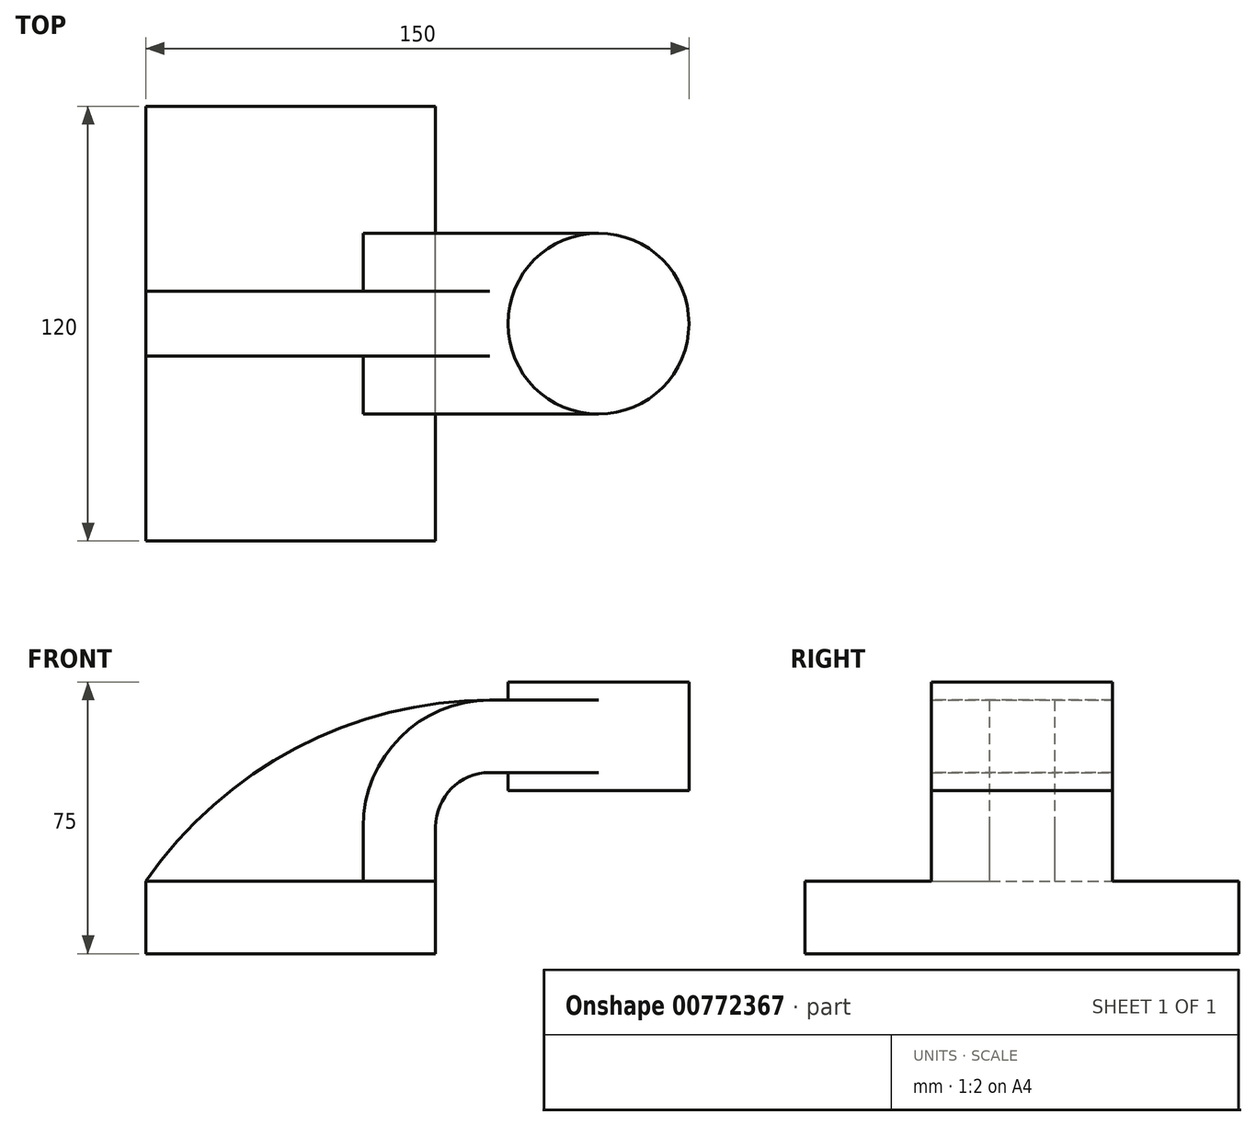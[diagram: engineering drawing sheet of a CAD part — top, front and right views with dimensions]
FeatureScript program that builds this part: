
annotation { "Feature Type Name" : "Feature", "Feature Type Description" : "" }
export const myFeature = defineFeature(function(context is Context, id is Id, definition is map)
    precondition{}
    {
        {
            var Q0;
            Q0=qCreatedBy(makeId("Front.planeOp"),FACE);
            var sketch = newSketch(context, id + "F0", { "sketchPlane" : qUnion([Q0])});
            skLineSegment(sketch, "E0", {"start": v(0, 0) * mm, "end": v(80, 0) * mm});
            skLineSegment(sketch, "E1", {"start": v(80, 0) * mm, "end": v(80, 20) * mm});
            skLineSegment(sketch, "E2", {"start": v(80, 20) * mm, "end": v(0, 20) * mm});
            skLineSegment(sketch, "E3", {"start": v(0, 20) * mm, "end": v(0, 0) * mm});
            skLineSegment(sketch, "E4", {"start": v(80, 20) * mm, "end": v(80, 35) * mm});
            skLineSegment(sketch, "E5", {"start": v(95, 50) * mm, "end": v(100, 50) * mm});
            skLineSegment(sketch, "E6", {"start": v(100, 50) * mm, "end": v(100, 45) * mm});
            skLineSegment(sketch, "E7", {"start": v(100, 45) * mm, "end": v(150, 45) * mm});
            skLineSegment(sketch, "E8", {"start": v(150, 45) * mm, "end": v(150, 75) * mm});
            skLineSegment(sketch, "E9", {"start": v(150, 75) * mm, "end": v(100, 75) * mm});
            skLineSegment(sketch, "E10", {"start": v(100, 75) * mm, "end": v(100, 70) * mm});
            skLineSegment(sketch, "E11", {"start": v(100, 70) * mm, "end": v(95, 70) * mm});
            skLineSegment(sketch, "E12", {"start": v(60, 35) * mm, "end": v(60, 20) * mm});
            skLineSegment(sketch, "E13", {"start": v(125, 75) * mm, "end": v(125, 45) * mm});
            skArc(sketch, "E14.filletArc", {"start": v(95, 70) * mm, "mid": v(70.25, 59.75) * mm, "end": v(60, 35) * mm});
            skPoint(sketch, "E15.visualSharp", {"position": v(80, 50) * mm});
            skArc(sketch, "E15.filletArc", {"start": v(95, 50) * mm, "mid": v(84.4, 45.6) * mm, "end": v(80, 35) * mm});
            skArc(sketch, "E16", {"start": v(95, 70) * mm, "mid": v(41.32, 56.74) * mm, "end": v(0, 20) * mm});
            skLineSegment(sketch, "E17", {"start": v(100, 70) * mm, "end": v(125, 70) * mm});
            skLineSegment(sketch, "E18", {"start": v(100, 50) * mm, "end": v(125, 50) * mm});
            skSolve(sketch);
        }
        {
            var Q0;
            Q0=makeQuery(id+"F0.imprint","IMPRINT",FACE,{"disambiguationData":[TD([[makeQuery(id+"F0.imprint","IMPRINT",EDGE,{"derivedFrom":sQuery(id+"F0.wireOp",EDGE,"E0")}),1.0]])]});
            extrude(context, id + "F1", {"entities" : qUnion([Q0]), "endBound" : BoundingType.SYMMETRIC, "depth" : 120 * mm, "offsetDistance" : 25 * mm});
        }
        {
            var Q0;
            {var subQ3=sQuery(id+"F0.wireOp",EDGE,"E4");Q0=makeQuery(id+"F0.imprint","IMPRINT",FACE,{"disambiguationData":[TD([[makeQuery(id+"F0.imprint","IMPRINT",EDGE,{"derivedFrom":subQ3}),1.0]])]});}
            extrude(context, id + "F2", {"entities" : qUnion([Q0]), "operationType" : NewBodyOperationType.ADD, "endBound" : BoundingType.SYMMETRIC, "depth" : 50 * mm, "offsetDistance" : 25 * mm});
        }
        {
            var Q0;
            {var subQ2=sQuery(id+"F0.wireOp",EDGE,"E12");Q0=makeQuery(id+"F0.imprint","IMPRINT",FACE,{"disambiguationData":[TD([[makeQuery(id+"F0.imprint","IMPRINT",EDGE,{"derivedFrom":subQ2}),-1.0]])]});}
            extrude(context, id + "F3", {"entities" : qUnion([Q0]), "operationType" : NewBodyOperationType.ADD, "endBound" : BoundingType.SYMMETRIC, "depth" : 18 * mm, "offsetDistance" : 25 * mm});
        }
        {
            var Q0;
            {var subQ4=sQuery(id+"F0.wireOp",EDGE,"E8");Q0=makeQuery(id+"F0.imprint","IMPRINT",FACE,{"disambiguationData":[TD([[makeQuery(id+"F0.imprint","IMPRINT",EDGE,{"derivedFrom":subQ4}),1.0]])]});}
            var Q1;
            Q1=sQuery(id+"F0.wireOp",EDGE,"E13");
            revolve(context, id + "F4", {"operationType" : NewBodyOperationType.ADD, "surfaceOperationType" : NewSurfaceOperationType.NEW, "entities" : qUnion([Q0]), "axis" : qUnion([Q1]), "revolveType" : RevolveType.FULL});
        }
    });
